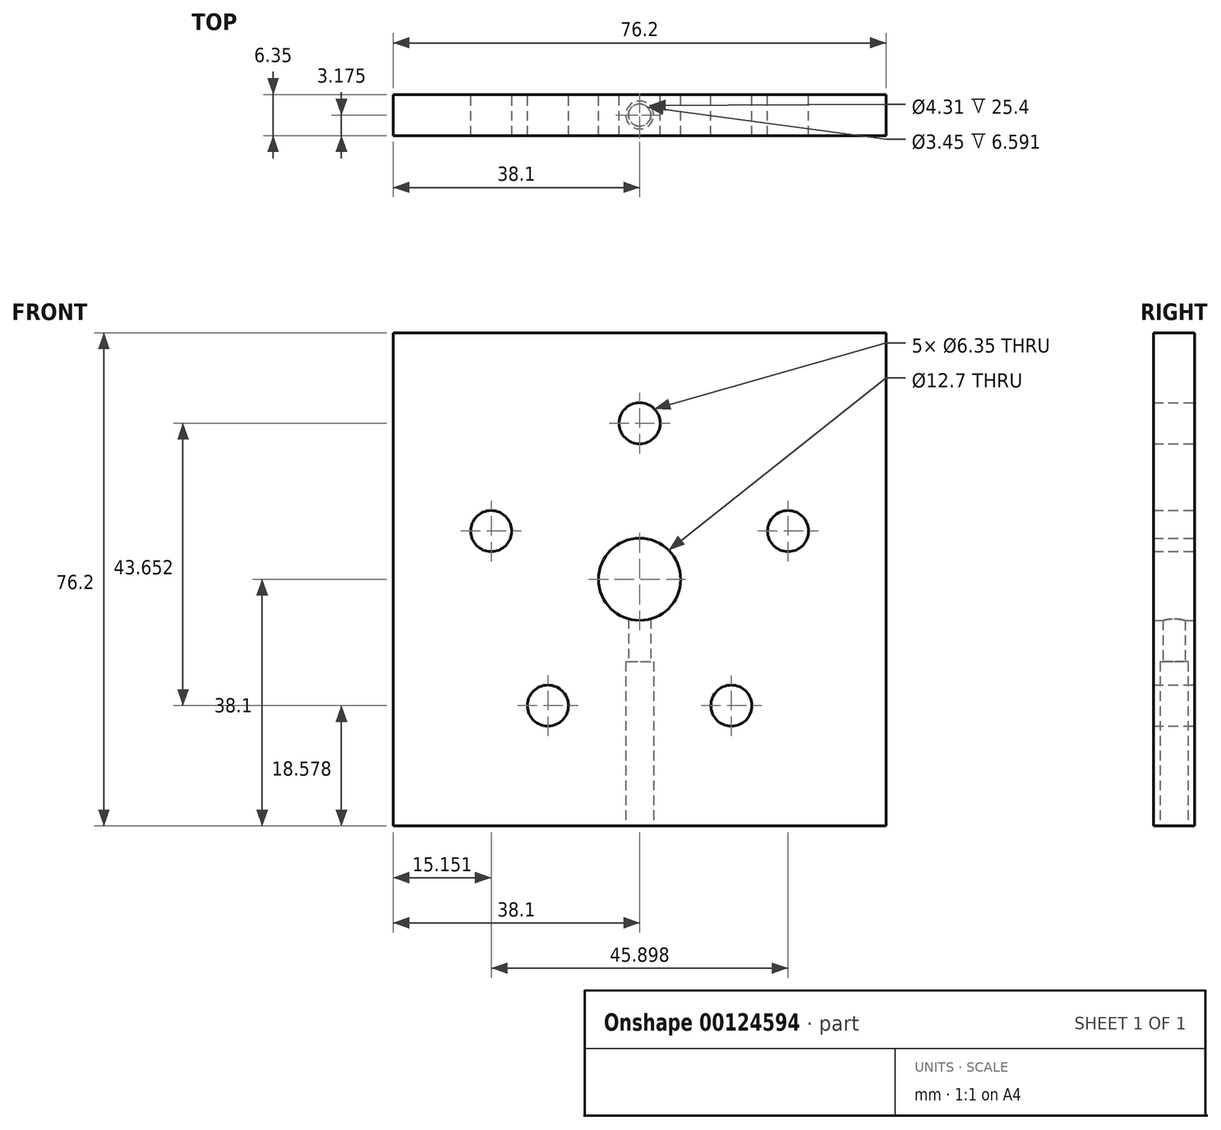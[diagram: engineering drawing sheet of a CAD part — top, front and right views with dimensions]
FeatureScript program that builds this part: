
annotation { "Feature Type Name" : "Feature", "Feature Type Description" : "" }
export const myFeature = defineFeature(function(context is Context, id is Id, definition is map)
    precondition{}
    {
        {
            var Q0;
            Q0=qCreatedBy(makeId("Front.planeOp"),FACE);
            var sketch = newSketch(context, id + "F0", { "sketchPlane" : qUnion([Q0])});
            skCircle(sketch, "E0", {"center": v(0, 0) * mm, "radius": 6.35 * mm});
            skLineSegment(sketch, "E1.bottom", {"start": v(38.1, -38.1) * mm, "end": v(-38.1, -38.1) * mm});
            skLineSegment(sketch, "E1.top", {"start": v(38.1, 38.1) * mm, "end": v(-38.1, 38.1) * mm});
            skLineSegment(sketch, "E1.left", {"start": v(38.1, -38.1) * mm, "end": v(38.1, 38.1) * mm});
            skLineSegment(sketch, "E1.right", {"start": v(-38.1, -38.1) * mm, "end": v(-38.1, 38.1) * mm});
            skLineSegment(sketch, "E2", {"start": v(0, -38.1) * mm, "end": v(0, 38.1) * mm, "construction": true});
            skLineSegment(sketch, "E3", {"start": v(-38.1, 0) * mm, "end": v(38.1, 0) * mm, "construction": true});
            skPoint(sketch, "E4", {"position": v(0, 27.3) * mm});
            skPoint(sketch, "E5", {"position": v(0, -27.3) * mm});
            skLineSegment(sketch, "E6", {"start": v(-38.1, -38.1) * mm, "end": v(38.1, 38.1) * mm, "construction": true});
            skLineSegment(sketch, "E7", {"start": v(38.1, -38.1) * mm, "end": v(-38.1, 38.1) * mm, "construction": true});
            skPoint(sketch, "E8", {"position": v(-19.3, 19.3) * mm});
            skPoint(sketch, "E9", {"position": v(19.3, 19.3) * mm});
            skPoint(sketch, "E10", {"position": v(27.3, 0) * mm});
            skPoint(sketch, "E11", {"position": v(-27.3, 0) * mm});
            skPoint(sketch, "E12", {"position": v(-17.75, -17.75) * mm});
            skPoint(sketch, "E13", {"position": v(19.3, -19.3) * mm});
            skCircle(sketch, "E14", {"center": v(0, 0) * mm, "radius": 27.3 * mm, "construction": true});
            skCircle(sketch, "E15", {"center": v(0, 24.13) * mm, "radius": 3.18 * mm});
            skCircle(sketch, "E16.1.0", {"center": v(-22.95, 7.46) * mm, "radius": 3.18 * mm});
            skCircle(sketch, "E16.2.0", {"center": v(-14.18, -19.52) * mm, "radius": 3.18 * mm});
            skCircle(sketch, "E16.3.0", {"center": v(14.18, -19.52) * mm, "radius": 3.18 * mm});
            skCircle(sketch, "E16.4.0", {"center": v(22.95, 7.46) * mm, "radius": 3.18 * mm});
            skSolve(sketch);
        }
        {
            var Q0;
            Q0=makeQuery(id+"F0.imprint","IMPRINT",FACE,{"disambiguationData":[TD([[makeQuery(id+"F0.imprint","IMPRINT",EDGE,{"derivedFrom":sQuery(id+"F0.wireOp",EDGE,"E0")}),-1.0]])]});
            extrude(context, id + "F1", {"entities" : qUnion([Q0]), "depth" : 6.35 * mm});
        }
        {
            var Q0;
            Q0=makeQuery(id+"F1.opExtrude","SWEPT_FACE",FACE,{"disambiguationData":[OSD([sQuery(id+"F0.wireOp",EDGE,"E1.bottom")])]});
            var sketch = newSketch(context, id + "F2", { "sketchPlane" : qUnion([Q0])});
            skLineSegment(sketch, "E17", {"start": v(0, 0) * mm, "end": v(0, 6.35) * mm, "construction": true});
            skCircle(sketch, "E18", {"center": v(0, 3.18) * mm, "radius": 2.15 * mm});
            skSolve(sketch);
        }
        {
            var Q0;
            Q0 = qSketchRegion(id + "F2", true);
            extrude(context, id + "F3", {"entities" : qUnion([Q0]), "operationType" : NewBodyOperationType.REMOVE, "oppositeDirection" : true, "depth" : 25.4 * mm});
        }
        {
            var Q0;
            Q0=makeQuery(id+"F1.opExtrude","SWEPT_FACE",FACE,{"disambiguationData":[OSD([sQuery(id+"F0.wireOp",EDGE,"E1.bottom")])]});
            var sketch = newSketch(context, id + "F4", { "sketchPlane" : qUnion([Q0])});
            skCircle(sketch, "E19", {"center": v(0, 3.18) * mm, "radius": 1.73 * mm});
            skSolve(sketch);
        }
        {
            var Q0;
            Q0 = qSketchRegion(id + "F4", true);
            var Q1;
            Q1=makeQuery(id+"F1.opExtrude","SWEPT_FACE",FACE,{"disambiguationData":[OSD([sQuery(id+"F0.wireOp",EDGE,"E0")])]});
            extrude(context, id + "F5", {"entities" : qUnion([Q0]), "operationType" : NewBodyOperationType.REMOVE, "endBound" : BoundingType.UP_TO_SURFACE, "oppositeDirection" : true, "endBoundEntityFace" : qUnion([Q1]), "depth" : 25.4 * mm});
        }
    });
